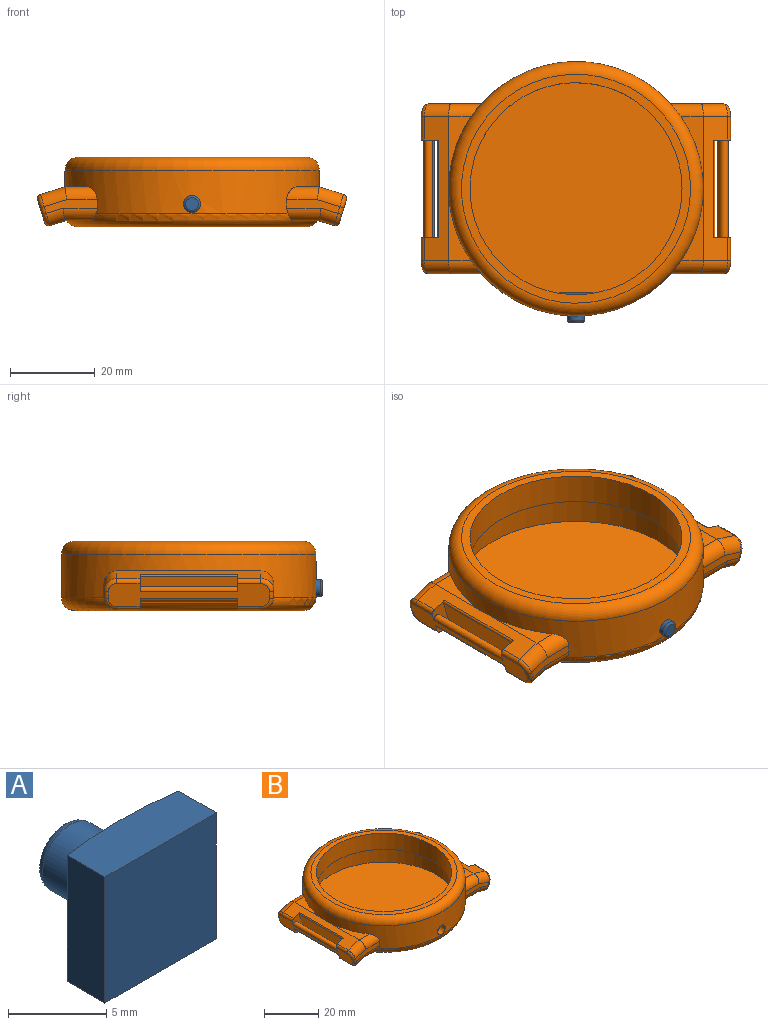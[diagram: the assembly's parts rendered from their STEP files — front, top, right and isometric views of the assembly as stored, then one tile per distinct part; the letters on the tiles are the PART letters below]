
ASSEMBLY  parts=2 mates=1
PART A: 9 faces, bbox 8x7x7.8 mm
  f0: cylinder r=27.5mm len=8mm, axis (0,0,-1), area 50.6mm2, adj f1,f2,f3,f5,f6
  f1: plane 8x3mm, normal (0,0,1), area 23.2mm2, adj f0,f3,f4,f5
  f2: plane 8x3mm, normal (0,0,-1), area 23.2mm2, adj f0,f3,f4,f5
  f3: plane 7.84x2.71mm, normal (1,0,0), area 21.2mm2, adj f0,f1,f2,f4
  f4: plane 8x7.84mm, normal (0,-1,0), area 62.7mm2, adj f1,f2,f3,f5
  f5: plane 7.84x2.71mm, normal (-1,0,0), area 21.2mm2, adj f0,f1,f2,f4
  f6: cylinder r=1.98mm len=3.97mm, axis (0,-1,0), area 44.1mm2, adj f0,f8
  f7: plane 2.97x2.97mm, normal (0,1,0), area 6.9mm2, adj f8
  f8: torus R=1.49mm, axis (0,-1,0), area 8.9mm2, adj f6,f7
PART B: 78 faces, bbox 72.9x64.9x16.4 mm
  f0: cylinder r=30mm len=60mm, axis (0,0,-1), area 1394.7mm2, adj f10,f11,f13,f14,f20,f22,f23,f24
  f1: cylinder r=27.5mm len=55mm, axis (0,0,-1), area 1283.3mm2, adj f67,f68,f77
  f2: plane 34x3.49mm, normal (-0.29,0,-0.96), area 43.8mm2, adj f4,f21,f36,f42,f48,f50,f55,f73
  f3: plane 38x5.4mm, normal (0.96,0,-0.29), area 119.2mm2, adj f4,f6,f48,f50,f51,f52,f53,f54
  f4: cylinder r=1mm len=5.5mm, axis (0,1,0), area 8.6mm2, adj f2,f3,f50,f53
  f5: plane 34x5.74mm, normal (0.29,0,0.96), area 123.5mm2, adj f6,f22,f24,f38,f40,f48,f50,f54
  f6: cylinder r=1mm len=5.5mm, axis (0,1,0), area 8.6mm2, adj f3,f5,f48,f56
  f7: plane 23x1.58mm, normal (0.96,0,0.29), area 37.9mm2, adj f45,f46,f71,f72
  f8: cylinder r=1mm len=5.5mm, axis (0,1,0), area 8.6mm2, adj f16,f17,f45,f65
  f9: cylinder r=1mm len=5.5mm, axis (0,1,0), area 8.6mm2, adj f15,f16,f46,f60
  f10: plane 17x5.28mm, normal (0,0,1), area 28.8mm2, adj f0,f15,f34
  f11: plane 17x5.28mm, normal (0,0,1), area 28.8mm2, adj f0,f15,f30
  f12: plane 34x5.87mm, normal (0,0,-1), area 75.1mm2, adj f17,f26,f29,f33
  f13: plane 12.5x3.2mm, normal (0,-1,0), area 23.2mm2, adj f0,f32,f33,f34,f35,f59
  f14: plane 12.5x3.2mm, normal (0,1,0), area 23.2mm2, adj f0,f28,f29,f30,f31,f66
  f15: plane 34x5.74mm, normal (-0.29,0,0.96), area 123.5mm2, adj f9,f10,f11,f31,f35,f45,f46,f62
  f16: plane 38x5.4mm, normal (-0.96,0,-0.29), area 119.2mm2, adj f8,f9,f45,f46,f59,f60,f61,f62
  f17: plane 34x3.49mm, normal (0.29,0,-0.96), area 43.8mm2, adj f8,f12,f28,f32,f45,f46,f63,f75
  f18: plane 54x54mm, normal (0,0,1), area 326.7mm2, adj f25,f27
  f19: plane 54x54mm, normal (0,0,-1), area 2290.2mm2, adj f26
  f20: plane 12.5x3.2mm, normal (0,-1,0), area 23.2mm2, adj f0,f36,f37,f38,f39,f51
  f21: plane 34x5.87mm, normal (0,0,-1), area 75.1mm2, adj f2,f26,f37,f43
  f22: plane 17x5.28mm, normal (0,0,1), area 28.8mm2, adj f0,f5,f39
  f23: plane 12.5x3.2mm, normal (0,1,0), area 23.2mm2, adj f0,f40,f41,f42,f43,f58
  f24: plane 17x5.28mm, normal (0,0,1), area 28.8mm2, adj f0,f5,f41
  f25: cylinder r=25mm len=50mm, axis (0,0,1), area 1146.7mm2, adj f18,f67
  f26: torus R=27mm, axis (0,0,1), area 714.5mm2, adj f0,f12,f19,f21,f29,f33,f37,f43
  f27: torus R=27mm, axis (0,0,1), area 856mm2, adj f0,f18
  f28: cylinder r=3mm len=4.8mm, axis (0.96,0,0.29), area 18mm2, adj f14,f17,f29,f65
  f29: cylinder r=3mm len=8.09mm, axis (1,0,0), area 33.5mm2, adj f0,f12,f14,f26,f28
  f30: cylinder r=3mm len=7.64mm, axis (-1,0,0), area 31mm2, adj f0,f11,f14,f31
  f31: cylinder r=3mm len=6.62mm, axis (-0.96,0,-0.29), area 27.5mm2, adj f14,f15,f30,f64
  f32: cylinder r=3mm len=4.8mm, axis (-0.96,0,-0.29), area 18mm2, adj f13,f17,f33,f61
  f33: cylinder r=3mm len=8.09mm, axis (-1,0,0), area 33.5mm2, adj f0,f12,f13,f26,f32
  f34: cylinder r=3mm len=7.64mm, axis (1,0,0), area 31mm2, adj f0,f10,f13,f35
  f35: cylinder r=3mm len=6.62mm, axis (0.96,0,0.29), area 27.5mm2, adj f13,f15,f34,f60
  f36: cylinder r=3mm len=4.8mm, axis (-0.96,0,0.29), area 18mm2, adj f2,f20,f37,f53
  f37: cylinder r=3mm len=8.09mm, axis (-1,0,0), area 33.5mm2, adj f0,f20,f21,f26,f36
  f38: cylinder r=3mm len=6.62mm, axis (0.96,0,-0.29), area 27.5mm2, adj f5,f20,f39,f52
  f39: cylinder r=3mm len=7.64mm, axis (1,0,0), area 31mm2, adj f0,f20,f22,f38
  f40: cylinder r=3mm len=6.62mm, axis (-0.96,0,0.29), area 27.5mm2, adj f5,f23,f41,f56
  f41: cylinder r=3mm len=7.64mm, axis (-1,0,0), area 31mm2, adj f0,f23,f24,f40
  f42: cylinder r=3mm len=4.8mm, axis (0.96,0,-0.29), area 18mm2, adj f2,f23,f43,f57
  f43: cylinder r=3mm len=8.09mm, axis (1,0,0), area 33.5mm2, adj f0,f21,f23,f26,f42
  f44: plane 23x6.36mm, normal (-0.96,0,-0.29), area 152.9mm2, adj f45,f46,f75,f76
  f45: plane 8.38x6.3mm, normal (0,-1,0), area 23.8mm2, adj f7,f8,f15,f16,f17,f44,f62,f71
  f46: plane 8.38x6.3mm, normal (0,1,0), area 23.8mm2, adj f7,f9,f15,f16,f17,f44,f63,f71
  f47: plane 23x1.58mm, normal (-0.96,0,0.29), area 37.9mm2, adj f48,f50,f69,f70
  f48: plane 8.38x6.3mm, normal (0,-1,0), area 23.8mm2, adj f2,f3,f5,f6,f47,f49,f55,f69
  f49: plane 23x6.36mm, normal (0.96,0,-0.29), area 152.9mm2, adj f48,f50,f73,f74
  f50: plane 8.38x6.3mm, normal (0,1,0), area 23.8mm2, adj f2,f3,f4,f5,f47,f49,f54,f69
  f51: cylinder r=1mm len=1.87mm, axis (-0.29,0,-0.96), area 2.6mm2, adj f3,f20,f52,f53
  f52: torus R=2mm, axis (0.96,0,-0.29), area 6.5mm2, adj f3,f38,f51,f54
  f53: torus R=2mm, axis (0.96,0,-0.29), area 6.5mm2, adj f3,f4,f36,f51
  f54: cylinder r=1mm len=5.5mm, axis (0,1,0), area 8.6mm2, adj f3,f5,f50,f52
  f55: cylinder r=1mm len=5.5mm, axis (0,1,0), area 8.6mm2, adj f2,f3,f48,f57
  f56: torus R=2mm, axis (0.96,0,-0.29), area 6.5mm2, adj f3,f6,f40,f58
  f57: torus R=2mm, axis (0.96,0,-0.29), area 6.5mm2, adj f3,f42,f55,f58
  f58: cylinder r=1mm len=1.87mm, axis (0.29,0,0.96), area 2.6mm2, adj f3,f23,f56,f57
  f59: cylinder r=1mm len=1.87mm, axis (-0.29,0,0.96), area 2.6mm2, adj f13,f16,f60,f61
  f60: torus R=2mm, axis (0.96,0,0.29), area 6.5mm2, adj f9,f16,f35,f59
  f61: torus R=2mm, axis (0.96,0,0.29), area 6.5mm2, adj f16,f32,f59,f63
  f62: cylinder r=1mm len=5.5mm, axis (0,1,0), area 8.6mm2, adj f15,f16,f45,f64
  f63: cylinder r=1mm len=5.5mm, axis (0,1,0), area 8.6mm2, adj f16,f17,f46,f61
  f64: torus R=2mm, axis (0.96,0,0.29), area 6.5mm2, adj f16,f31,f62,f66
  f65: torus R=2mm, axis (0.96,0,0.29), area 6.5mm2, adj f8,f16,f28,f66
  f66: cylinder r=1mm len=1.87mm, axis (0.29,0,-0.96), area 2.6mm2, adj f14,f16,f64,f65
  f67: plane 55x55mm, normal (0,0,-1), area 412.3mm2, adj f1,f25
  f68: plane 55x55mm, normal (0,0,1), area 2375.8mm2, adj f1
  f69: cylinder r=1mm len=23mm, axis (0,1,0), area 72.3mm2, adj f3,f47,f48,f50
  f70: cylinder r=1mm len=23mm, axis (0,1,0), area 72.3mm2, adj f3,f47,f48,f50
  f71: cylinder r=1mm len=23mm, axis (0,1,0), area 72.3mm2, adj f7,f16,f45,f46
  f72: cylinder r=1mm len=23mm, axis (0,1,0), area 72.3mm2, adj f7,f16,f45,f46
  f73: cylinder r=0.5mm len=23mm, axis (0,-1,0), area 18.1mm2, adj f2,f48,f49,f50
  f74: cylinder r=0.5mm len=23mm, axis (0,1,0), area 18.1mm2, adj f5,f48,f49,f50
  f75: cylinder r=0.5mm len=23mm, axis (0,1,0), area 18.1mm2, adj f17,f44,f45,f46
  f76: cylinder r=0.5mm len=23mm, axis (0,1,0), area 18.1mm2, adj f15,f44,f45,f46
  f77: cylinder r=2mm len=4mm, axis (0,1,0), area 31.5mm2, adj f0,f1
PLACE A rot(axis=(0,0,1),180deg) t=(-1.8,-24.63,-4.15)mm
PLACE B t=(-1.8,-0.13,-0.15)mm
MATE slider A.f6 <-> B.f77  axis (0,1,0) through (-1.8,-27.54,-4.15)mm
